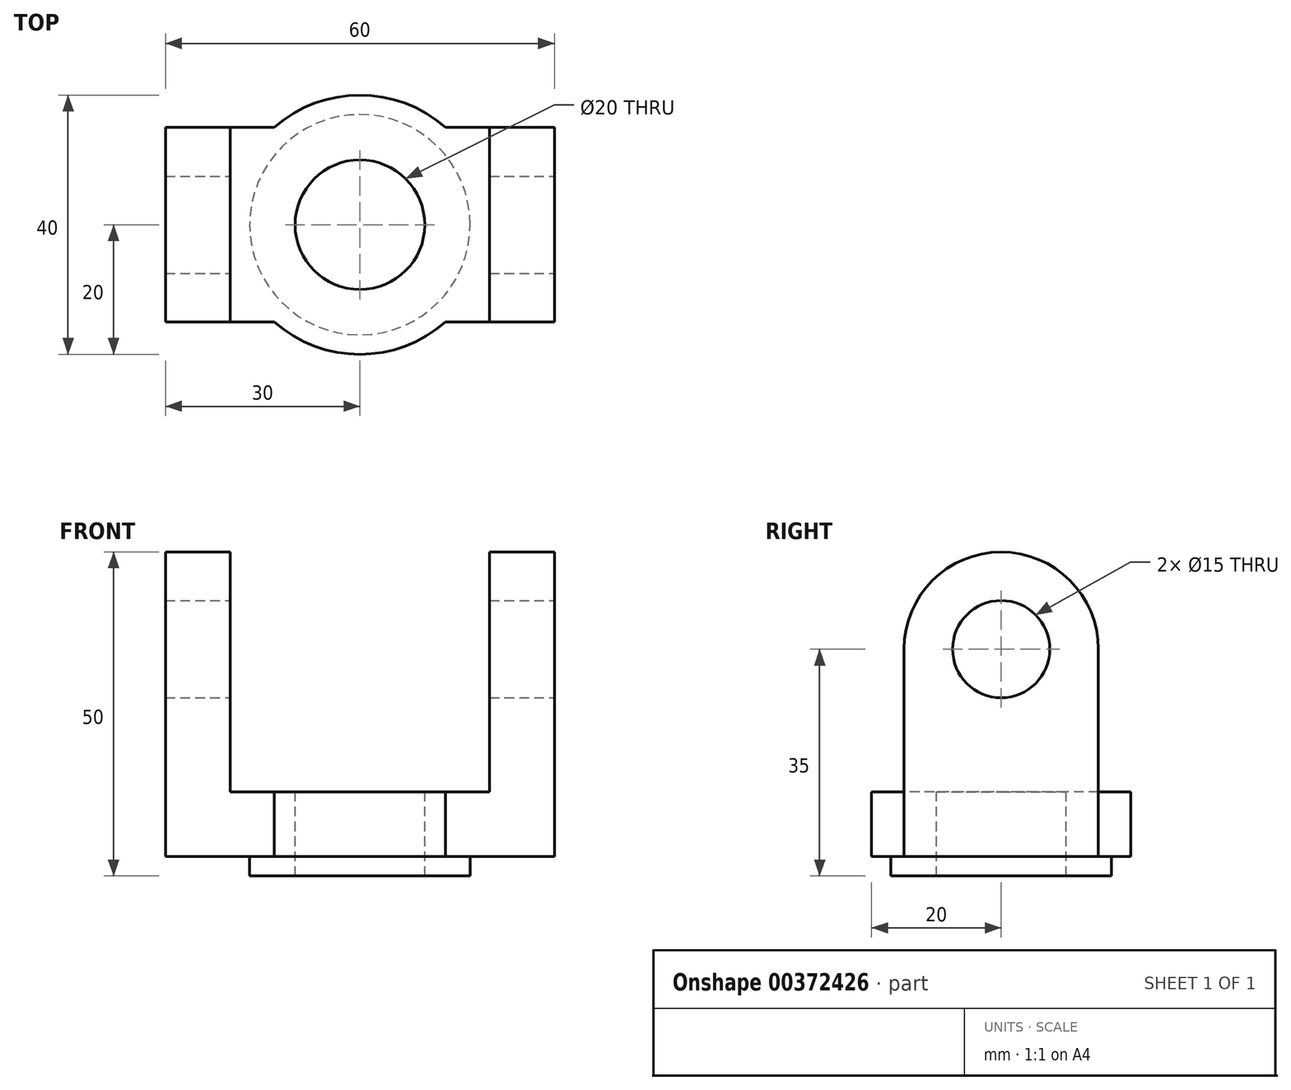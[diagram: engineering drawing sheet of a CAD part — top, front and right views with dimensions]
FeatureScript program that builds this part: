
annotation { "Feature Type Name" : "Feature", "Feature Type Description" : "" }
export const myFeature = defineFeature(function(context is Context, id is Id, definition is map)
    precondition{}
    {
        {
            var Q0;
            Q0=qCreatedBy(makeId("Top.planeOp"),FACE);
            var sketch = newSketch(context, id + "F0", { "sketchPlane" : qUnion([Q0])});
            skCircle(sketch, "E0", {"center": v(0, 0) * mm, "radius": 20 * mm});
            skCircle(sketch, "E1", {"center": v(0, 0) * mm, "radius": 10 * mm});
            skSolve(sketch);
        }
        {
            var Q0;
            Q0 = qSketchRegion(id + "F0", true);
            extrude(context, id + "F1", {"entities" : qUnion([Q0]), "depth" : 10 * mm});
        }
        {
            var Q0;
            Q0=qCreatedBy(makeId("Top.planeOp"),FACE);
            var sketch = newSketch(context, id + "F2", { "sketchPlane" : qUnion([Q0])});
            skLineSegment(sketch, "E2", {"start": v(-30, 15) * mm, "end": v(-30, -15) * mm});
            skLineSegment(sketch, "E3", {"start": v(-30, -15) * mm, "end": v(30, -15) * mm});
            skLineSegment(sketch, "E4", {"start": v(30, -15) * mm, "end": v(30, 15) * mm});
            skLineSegment(sketch, "E5", {"start": v(30, 15) * mm, "end": v(-30, 15) * mm});
            skSolve(sketch);
        }
        {
            var Q0;
            Q0 = qSketchRegion(id + "F2", true);
            extrude(context, id + "F3", {"entities" : qUnion([Q0]), "operationType" : NewBodyOperationType.ADD, "depth" : 10 * mm});
        }
        {
            var Q0;
            Q0=makeQuery(id+"F3.boolean.opBoolean","MERGE",FACE,{"derivedFrom":[makeQuery(id+"F1.opExtrude","CAP_FACE",FACE,{"disambiguationData":[OSD([sQuery(id+"F0.wireOp",EDGE,"E0"),sQuery(id+"F0.wireOp",EDGE,"E1")])],"isStart":false}),makeQuery(id+"F3.opExtrude","CAP_FACE",FACE,{"disambiguationData":[OSD([sQuery(id+"F2.wireOp",EDGE,"E2"),sQuery(id+"F2.wireOp",EDGE,"E3"),sQuery(id+"F2.wireOp",EDGE,"E4"),sQuery(id+"F2.wireOp",EDGE,"E5")])],"isStart":false})]});
            var sketch = newSketch(context, id + "F4", { "sketchPlane" : qUnion([Q0])});
            skCircle(sketch, "E6", {"center": v(0, 0) * mm, "radius": 17 * mm});
            skSolve(sketch);
        }
        {
            var Q0;
            Q0 = qSketchRegion(id + "F4", true);
            extrude(context, id + "F5", {"entities" : qUnion([Q0]), "operationType" : NewBodyOperationType.ADD, "oppositeDirection" : true, "depth" : 13 * mm});
        }
        {
            var Q0;
            Q0=makeQuery(id+"F3.boolean.opBoolean","MERGE",FACE,{"derivedFrom":[makeQuery(id+"F1.opExtrude","CAP_FACE",FACE,{"disambiguationData":[OSD([sQuery(id+"F0.wireOp",EDGE,"E0"),sQuery(id+"F0.wireOp",EDGE,"E1")])],"isStart":false}),makeQuery(id+"F3.opExtrude","CAP_FACE",FACE,{"disambiguationData":[OSD([sQuery(id+"F2.wireOp",EDGE,"E2"),sQuery(id+"F2.wireOp",EDGE,"E3"),sQuery(id+"F2.wireOp",EDGE,"E4"),sQuery(id+"F2.wireOp",EDGE,"E5")])],"isStart":false})]});
            var sketch = newSketch(context, id + "F6", { "sketchPlane" : qUnion([Q0])});
            skCircle(sketch, "E7", {"center": v(0, 0) * mm, "radius": 10 * mm});
            skSolve(sketch);
        }
        {
            var Q0;
            Q0 = qSketchRegion(id + "F6", true);
            extrude(context, id + "F7", {"entities" : qUnion([Q0]), "operationType" : NewBodyOperationType.REMOVE, "endBound" : BoundingType.THROUGH_ALL, "oppositeDirection" : true, "depth" : 25 * mm});
        }
        {
            var Q0;
            Q0=makeQuery(id+"F3.opExtrude","SWEPT_FACE",FACE,{"disambiguationData":[OSD([sQuery(id+"F2.wireOp",EDGE,"E4")])]});
            var sketch = newSketch(context, id + "F8", { "sketchPlane" : qUnion([Q0])});
            skLineSegment(sketch, "E8", {"start": v(-15, 0) * mm, "end": v(-15, 66) * mm});
            skLineSegment(sketch, "E9", {"start": v(15, 66) * mm, "end": v(15, 0) * mm});
            skLineSegment(sketch, "E10", {"start": v(15, 0) * mm, "end": v(-15, 0) * mm});
            skLineSegment(sketch, "E11", {"start": v(-15, 66) * mm, "end": v(15, 66) * mm});
            skSolve(sketch);
        }
        {
            var Q0;
            Q0 = qSketchRegion(id + "F8", true);
            extrude(context, id + "F9", {"entities" : qUnion([Q0]), "operationType" : NewBodyOperationType.ADD, "oppositeDirection" : true, "depth" : 60 * mm});
        }
        {
            var Q0;
            {var subQ1=sQuery(id+"F2.wireOp",EDGE,"E4");var subQ2=sQuery(id+"F2.wireOp",EDGE,"E3");var subQ3=sQuery(id+"F2.wireOp",EDGE,"E2");var subQ11=makeQuery(id+"F3.opExtrude","SWEPT_FACE",FACE,{"disambiguationData":[OSD([subQ2])]});Q0=makeQuery(id+"F9.boolean.opBoolean","MERGE",FACE,{"derivedFrom":[makeQuery(id+"F3.boolean.opBoolean","SPLIT",FACE,{"disambiguationData":[TD([makeQuery(id+"F3.opExtrude","SWEPT_FACE",FACE,{"disambiguationData":[OSD([subQ3])]})])],"derivedFrom":subQ11}),makeQuery(id+"F3.boolean.opBoolean","SPLIT",FACE,{"disambiguationData":[TD([makeQuery(id+"F3.opExtrude","SWEPT_FACE",FACE,{"disambiguationData":[OSD([subQ1])]})])],"derivedFrom":subQ11}),makeQuery(id+"F9.opExtrude","SWEPT_FACE",FACE,{"disambiguationData":[OSD([sQuery(id+"F8.wireOp",EDGE,"E8")])]})]});}
            var sketch = newSketch(context, id + "F10", { "sketchPlane" : qUnion([Q0])});
            skLineSegment(sketch, "E12", {"start": v(-20, 66) * mm, "end": v(-20, 10) * mm});
            skLineSegment(sketch, "E13", {"start": v(-20, 10) * mm, "end": v(20, 10) * mm});
            skPoint(sketch, "E13.endSnap0", {"position": v(0, 10) * mm});
            skLineSegment(sketch, "E14", {"start": v(20, 10) * mm, "end": v(20, 66) * mm});
            skLineSegment(sketch, "E15", {"start": v(20, 66) * mm, "end": v(-20, 66) * mm});
            skSolve(sketch);
        }
        {
            var Q0;
            Q0 = qSketchRegion(id + "F10", true);
            extrude(context, id + "F11", {"entities" : qUnion([Q0]), "operationType" : NewBodyOperationType.REMOVE, "endBound" : BoundingType.THROUGH_ALL, "oppositeDirection" : true, "depth" : 25 * mm});
        }
        {
            var Q0;
            Q0=makeQuery(id+"F9.boolean.opBoolean","MERGE",FACE,{"derivedFrom":[makeQuery(id+"F3.opExtrude","SWEPT_FACE",FACE,{"disambiguationData":[OSD([sQuery(id+"F2.wireOp",EDGE,"E4")])]}),makeQuery(id+"F9.opExtrude","CAP_FACE",FACE,{"disambiguationData":[OSD([sQuery(id+"F8.wireOp",EDGE,"E8"),sQuery(id+"F8.wireOp",EDGE,"E9"),sQuery(id+"F8.wireOp",EDGE,"E10"),sQuery(id+"F8.wireOp",EDGE,"E11")])],"isStart":true})]});
            var sketch = newSketch(context, id + "F12", { "sketchPlane" : qUnion([Q0])});
            skCircle(sketch, "E16", {"center": v(0, 32) * mm, "radius": 7.5 * mm});
            skArc(sketch, "E17", {"start": v(15, 32) * mm, "mid": v(0, 47) * mm, "end": v(-15, 32) * mm});
            skPoint(sketch, "E17.startSnap0", {"position": v(15, 33) * mm});
            skSolve(sketch);
        }
        {
            var Q0;
            Q0 = qSketchRegion(id + "F12", true);
            var Q1;
            {var subQ0=sQuery(id+"F12.wireOp",EDGE,"E17");Q1=makeQuery(id+"F12.imprint","IMPRINT",FACE,{"disambiguationData":[TD([[makeQuery(id+"F12.imprint","IMPRINT",EDGE,{"derivedFrom":subQ0}),-1.0]])]});}
            extrude(context, id + "F13", {"entities" : qUnion([Q0, Q1]), "operationType" : NewBodyOperationType.REMOVE, "endBound" : BoundingType.THROUGH_ALL, "oppositeDirection" : true, "depth" : 25 * mm});
        }
        {
            var Q0;
            {var subQ0=sQuery(id+"F0.wireOp",EDGE,"E0");var subQ2=sQuery(id+"F2.wireOp",EDGE,"E5");var subQ3=sQuery(id+"F2.wireOp",EDGE,"E3");var subQ4=makeQuery(id+"F3.boolean.opBoolean","MERGE",FACE,{"derivedFrom":[makeQuery(id+"F1.opExtrude","CAP_FACE",FACE,{"disambiguationData":[OSD([subQ0,sQuery(id+"F0.wireOp",EDGE,"E1")])],"isStart":false}),makeQuery(id+"F3.opExtrude","CAP_FACE",FACE,{"disambiguationData":[OSD([sQuery(id+"F2.wireOp",EDGE,"E2"),subQ3,sQuery(id+"F2.wireOp",EDGE,"E4"),subQ2])],"isStart":false})]});Q0=makeQuery(id+"F11.boolean.opBoolean","MERGE",FACE,{"derivedFrom":[makeQuery(id+"F9.boolean.opBoolean","SPLIT",FACE,{"disambiguationData":[TD([makeQuery(id+"F3.opExtrude","SWEPT_FACE",FACE,{"disambiguationData":[OSD([subQ3])]})])],"derivedFrom":subQ4}),makeQuery(id+"F9.boolean.opBoolean","SPLIT",FACE,{"disambiguationData":[TD([makeQuery(id+"F3.opExtrude","SWEPT_FACE",FACE,{"disambiguationData":[OSD([subQ2])]})])],"derivedFrom":subQ4}),makeQuery(id+"F11.opExtrude","SWEPT_FACE",FACE,{"disambiguationData":[OSD([sQuery(id+"F10.wireOp",EDGE,"E13")])]})]});}
            var sketch = newSketch(context, id + "F14", { "sketchPlane" : qUnion([Q0])});
            skCircle(sketch, "E18", {"center": v(0, 0) * mm, "radius": 10 * mm});
            skSolve(sketch);
        }
        {
            var Q0;
            Q0 = qSketchRegion(id + "F14", true);
            extrude(context, id + "F15", {"entities" : qUnion([Q0]), "operationType" : NewBodyOperationType.REMOVE, "endBound" : BoundingType.THROUGH_ALL, "oppositeDirection" : true, "depth" : 25 * mm});
        }
    });
